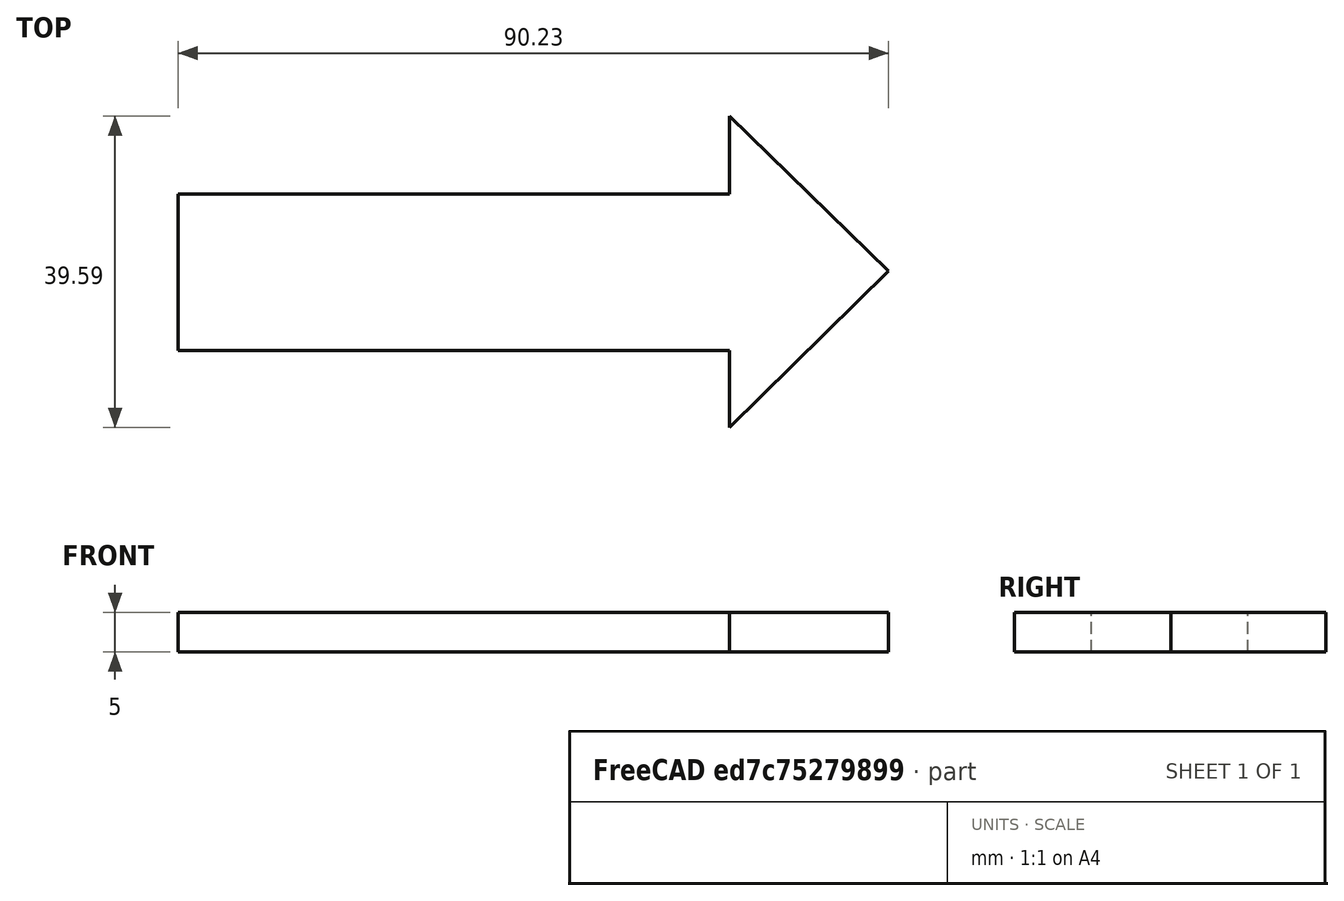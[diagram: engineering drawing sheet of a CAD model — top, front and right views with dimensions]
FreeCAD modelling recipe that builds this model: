
FCSTD DOCUMENT  (FreeCAD 0.21R33694 (Git))
Label: OJT1_T16R01_fletxa
License: All rights reserved
LicenseURL: http://en.wikipedia.org/wiki/All_rights_reserved
objects: Sketcher::SketchObject×1, PartDesign::Pad×1, PartDesign::Body×1
note: 4 computed .brp shape members not serialized (recipe doc carries the construction recipe); baked Part::Feature solids carry a one-line shape summary decoded from their .brp

FEATURE [Sketcher::SketchObject] Sketch
  FullyConstrained = false
  MapMode = 5
  Support = -> [XY_Plane]
  sketch-geometry (7):
    g0: LineSegment StartX=-30.0329 StartY=9.74807 StartZ=0 EndX=-30.0329 EndY=-10.1133 EndZ=0
    g1: LineSegment StartX=-30.0329 StartY=-10.1133 StartZ=0 EndX=40.0334 EndY=-10.1133 EndZ=0
    g2: LineSegment StartX=40.0334 StartY=-10.1133 StartZ=0 EndX=40.0334 EndY=-19.8991 EndZ=0
    g3: LineSegment StartX=40.0334 StartY=-19.8991 StartZ=0 EndX=60.1981 EndY=0 EndZ=0
    g4: LineSegment StartX=60.1981 StartY=0 StartZ=0 EndX=39.9825 EndY=19.6897 EndZ=0
    g5: LineSegment StartX=39.9825 StartY=19.6897 StartZ=0 EndX=39.9825 EndY=9.74807 EndZ=0
    g6: LineSegment StartX=-30.0329 StartY=9.74807 StartZ=0 EndX=39.9825 EndY=9.74807 EndZ=0
  constraints (13):
    c: Vertical(g0)
    c: Coincident(g0,g1)
    c: Horizontal(g1)
    c: Coincident(g1,g2)
    c: Vertical(g2)
    c: Coincident(g2,g3)
    c: PointOnObject(g3,g-1)
    c: Coincident(g3,g4)
    c: Coincident(g4,g5)
    c: Vertical(g5)
    c: Coincident(g0,g6)
    c: Coincident(g6,g5)
    c: Horizontal(g6)
FEATURE [PartDesign::Pad] Pad
  Direction = (0,0,1)
  Length = 5
  Length2 = 10
  Profile = -> Sketch
  ReferenceAxis = -> Sketch [N_Axis]
  Type = 0
FEATURE [PartDesign::Body] Body
  Group = -> [Sketch,Pad]
  Origin = -> Origin
  Tip = -> Pad
